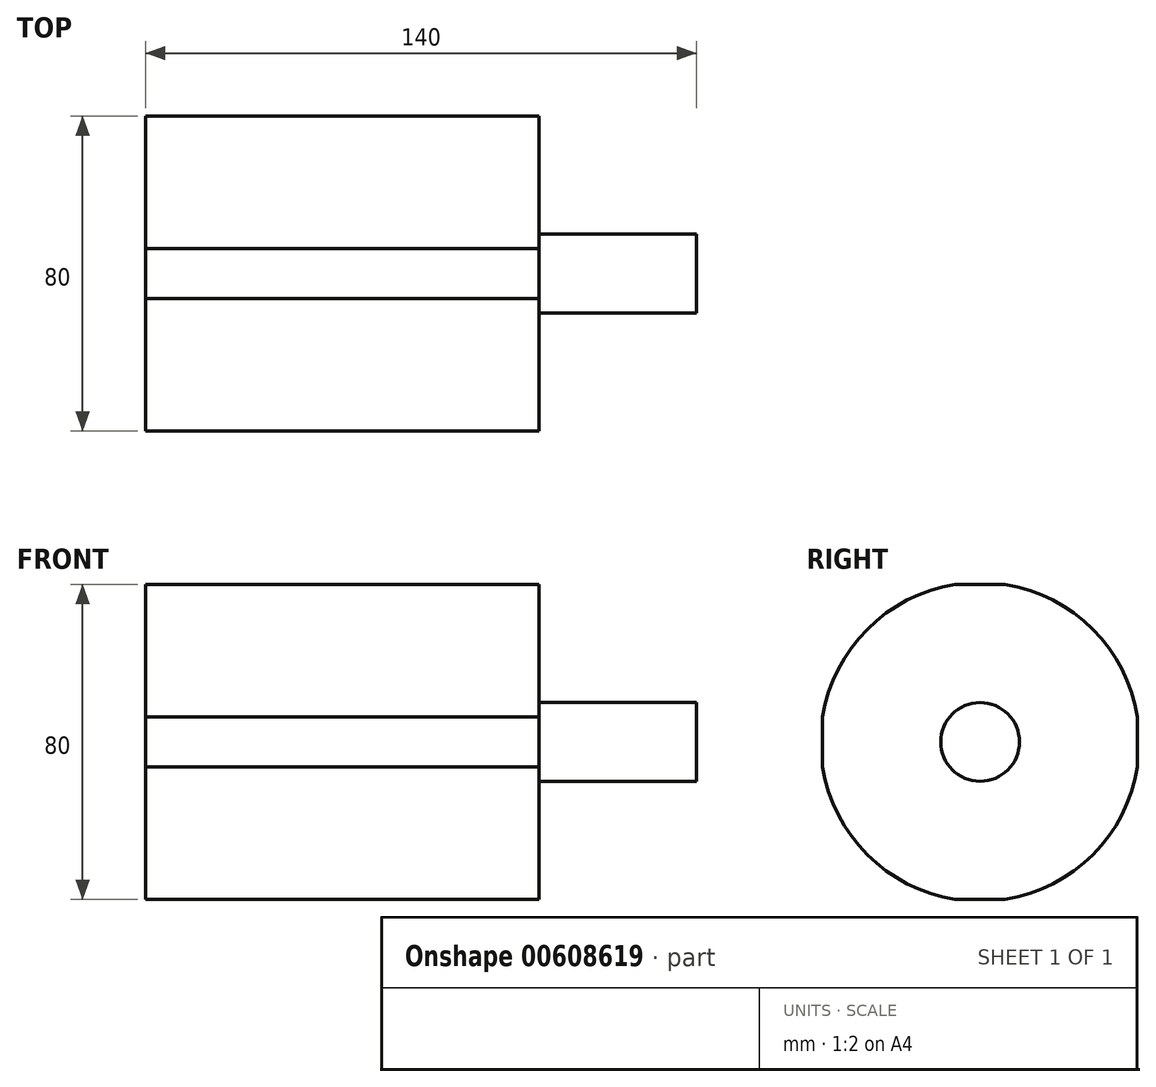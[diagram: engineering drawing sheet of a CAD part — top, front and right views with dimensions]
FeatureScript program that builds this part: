
annotation { "Feature Type Name" : "Feature", "Feature Type Description" : "" }
export const myFeature = defineFeature(function(context is Context, id is Id, definition is map)
    precondition{}
    {
        {
            var Q0;
            Q0=qCreatedBy(makeId("Right.planeOp"),FACE);
            var sketch = newSketch(context, id + "F0", { "sketchPlane" : qUnion([Q0])});
            skCircle(sketch, "E0", {"center": v(0, 0) * mm, "radius": 40.5 * mm});
            skSolve(sketch);
        }
        {
            var Q0;
            Q0=makeQuery(id+"F0.imprint","IMPRINT",FACE,{"disambiguationData":[TD([[makeQuery(id+"F0.imprint","IMPRINT",EDGE,{"derivedFrom":sQuery(id+"F0.wireOp",EDGE,"E0")}),1.0]])]});
            extrude(context, id + "F1", {"entities" : qUnion([Q0]), "depth" : 100 * mm, "offsetDistance" : 25 * mm});
        }
        {
            var Q0;
            Q0=makeQuery(id+"F1.opExtrude","CAP_FACE",FACE,{"disambiguationData":[OSD([sQuery(id+"F0.wireOp",EDGE,"E0")])],"isStart":false});
            var sketch = newSketch(context, id + "F2", { "sketchPlane" : qUnion([Q0])});
            skLineSegment(sketch, "E1.bottom", {"start": v(40, -40) * mm, "end": v(-40, -40) * mm});
            skLineSegment(sketch, "E1.top", {"start": v(40, 40) * mm, "end": v(-40, 40) * mm});
            skLineSegment(sketch, "E1.left", {"start": v(40, -40) * mm, "end": v(40, 40) * mm});
            skLineSegment(sketch, "E1.right", {"start": v(-40, -40) * mm, "end": v(-40, 40) * mm});
            skPoint(sketch, "E1.middle", {"position": v(0, 0) * mm});
            skLineSegment(sketch, "E2.bottom", {"start": v(45, -45) * mm, "end": v(-45, -45) * mm});
            skLineSegment(sketch, "E2.top", {"start": v(45, 45) * mm, "end": v(-45, 45) * mm});
            skLineSegment(sketch, "E2.left", {"start": v(45, -45) * mm, "end": v(45, 45) * mm});
            skLineSegment(sketch, "E2.right", {"start": v(-45, -45) * mm, "end": v(-45, 45) * mm});
            skSolve(sketch);
        }
        {
            var Q0;
            {var subQ1=sQuery(id+"F2.wireOp",EDGE,"E1.left");Q0=makeQuery(id+"F2.imprint","IMPRINT",FACE,{"disambiguationData":[TD([[makeQuery(id+"F2.imprint","IMPRINT",EDGE,{"derivedFrom":subQ1}),-1.0]])]});}
            var Q1;
            {var subQ0=sQuery(id+"F2.wireOp",EDGE,"E1.top");var subQ1=makeQuery(id+"F1.opExtrude","CAP_EDGE",EDGE,{"disambiguationData":[OSD([sQuery(id+"F0.wireOp",EDGE,"E0")])],"isStart":false});var subQ2=makeQuery(id+"F2.imprint","INTERSECT",VERTEX,{"disambiguationData":[OD(0.0)],"derivedFrom":[subQ1,subQ0]});Q1=makeQuery(id+"F2.imprint","IMPRINT",FACE,{"disambiguationData":[TD([[makeQuery(id+"F2.imprint","IMPRINT",EDGE,{"disambiguationData":[TD([[subQ2,-1.0]])],"derivedFrom":subQ0}),-1.0]])]});}
            var Q2;
            {var subQ0=sQuery(id+"F2.wireOp",EDGE,"E1.bottom");var subQ1=makeQuery(id+"F1.opExtrude","CAP_EDGE",EDGE,{"disambiguationData":[OSD([sQuery(id+"F0.wireOp",EDGE,"E0")])],"isStart":false});var subQ2=makeQuery(id+"F2.imprint","INTERSECT",VERTEX,{"disambiguationData":[OD(0.0)],"derivedFrom":[subQ1,subQ0]});Q2=makeQuery(id+"F2.imprint","IMPRINT",FACE,{"disambiguationData":[TD([[makeQuery(id+"F2.imprint","IMPRINT",EDGE,{"disambiguationData":[TD([[subQ2,-1.0]])],"derivedFrom":subQ0}),1.0]])]});}
            var Q3;
            {var subQ0=sQuery(id+"F2.wireOp",EDGE,"E1.right");var subQ1=makeQuery(id+"F1.opExtrude","CAP_EDGE",EDGE,{"disambiguationData":[OSD([sQuery(id+"F0.wireOp",EDGE,"E0")])],"isStart":false});var subQ2=makeQuery(id+"F2.imprint","INTERSECT",VERTEX,{"disambiguationData":[OD(0.0)],"derivedFrom":[subQ1,subQ0]});Q3=makeQuery(id+"F2.imprint","IMPRINT",FACE,{"disambiguationData":[TD([[makeQuery(id+"F2.imprint","IMPRINT",EDGE,{"disambiguationData":[TD([[subQ2,-1.0]])],"derivedFrom":subQ0}),1.0]])]});}
            extrude(context, id + "F3", {"entities" : qUnion([Q0, Q1, Q2, Q3]), "operationType" : NewBodyOperationType.REMOVE, "endBound" : BoundingType.THROUGH_ALL, "oppositeDirection" : true, "depth" : 25 * mm, "offsetDistance" : 25 * mm});
        }
        {
            var Q0;
            Q0=makeQuery(id+"F1.opExtrude","CAP_FACE",FACE,{"disambiguationData":[OSD([sQuery(id+"F0.wireOp",EDGE,"E0")])],"isStart":false});
            var sketch = newSketch(context, id + "F4", { "sketchPlane" : qUnion([Q0])});
            skCircle(sketch, "E3", {"center": v(0, 0) * mm, "radius": 10 * mm});
            skSolve(sketch);
        }
        {
            var Q0;
            Q0=makeQuery(id+"F4.imprint","IMPRINT",FACE,{"disambiguationData":[TD([[makeQuery(id+"F4.imprint","IMPRINT",EDGE,{"derivedFrom":sQuery(id+"F4.wireOp",EDGE,"E3")}),1.0]])]});
            extrude(context, id + "F5", {"entities" : qUnion([Q0]), "operationType" : NewBodyOperationType.ADD, "depth" : 40 * mm, "offsetDistance" : 25 * mm});
        }
    });
